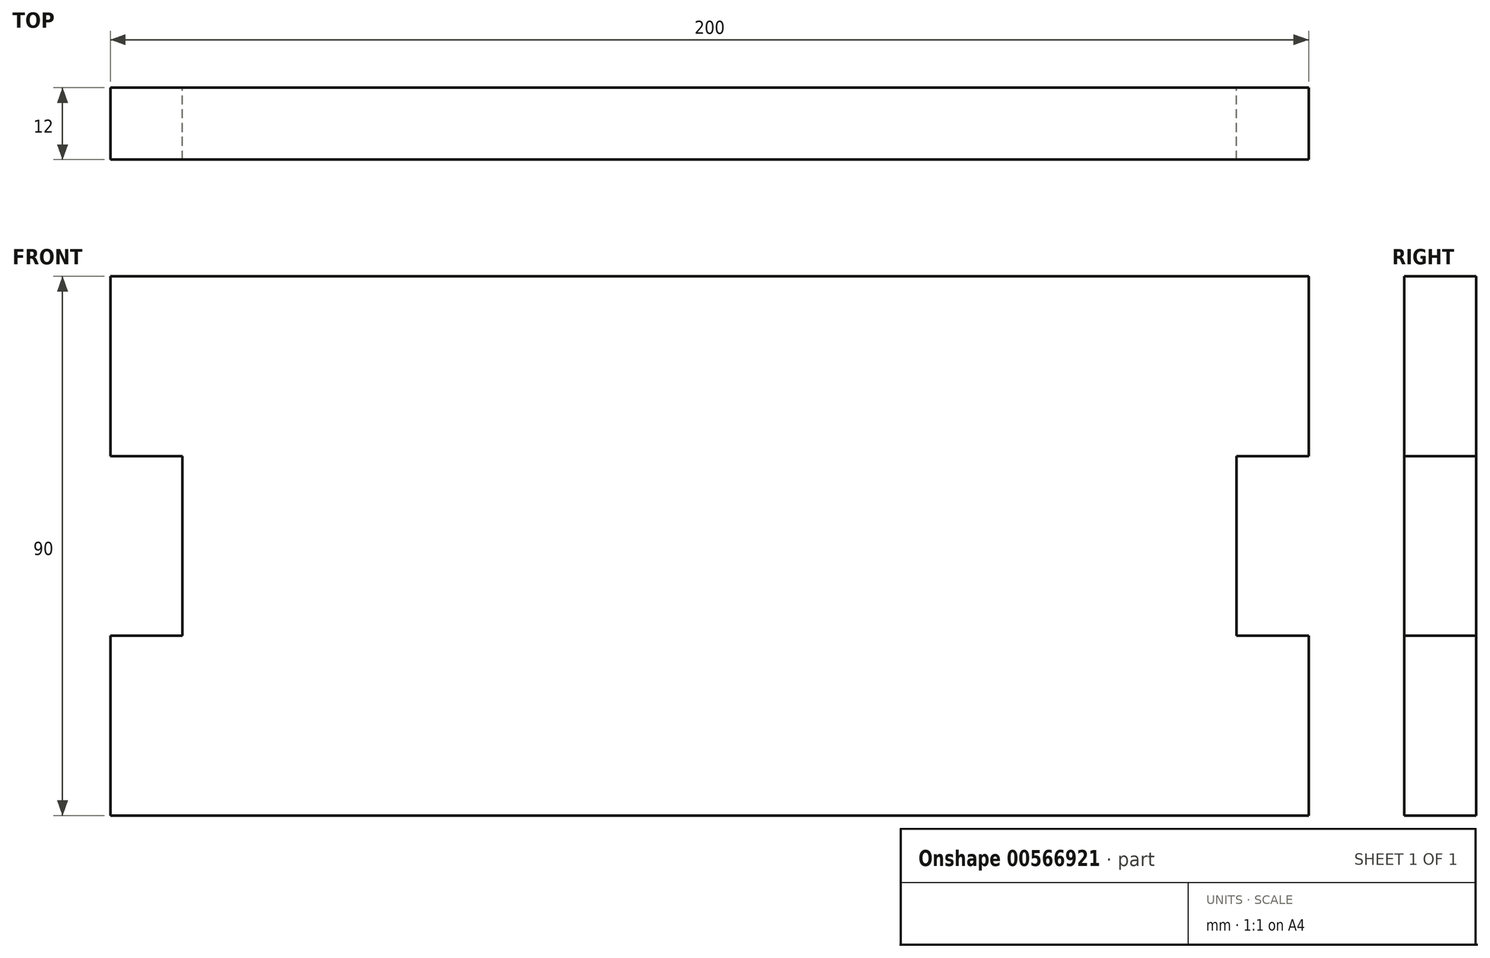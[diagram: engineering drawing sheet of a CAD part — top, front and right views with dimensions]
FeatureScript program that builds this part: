
annotation { "Feature Type Name" : "Feature", "Feature Type Description" : "" }
export const myFeature = defineFeature(function(context is Context, id is Id, definition is map)
    precondition{}
    {
        {
            var Q0;
            Q0=qCreatedBy(makeId("Front.planeOp"),FACE);
            var sketch = newSketch(context, id + "F0", { "sketchPlane" : qUnion([Q0])});
            skLineSegment(sketch, "E0", {"start": v(0, 0) * mm, "end": v(0, 30) * mm});
            skLineSegment(sketch, "E1", {"start": v(0, 30) * mm, "end": v(12, 30) * mm});
            skLineSegment(sketch, "E2", {"start": v(12, 30) * mm, "end": v(12, 60) * mm});
            skLineSegment(sketch, "E3", {"start": v(12, 60) * mm, "end": v(0, 60) * mm});
            skLineSegment(sketch, "E4", {"start": v(0, 60) * mm, "end": v(0, 90) * mm});
            skLineSegment(sketch, "E5", {"start": v(0, 90) * mm, "end": v(100, 90) * mm});
            skLineSegment(sketch, "E6", {"start": v(100, 90) * mm, "end": v(100, 0) * mm, "construction": true});
            skLineSegment(sketch, "E7", {"start": v(100, 0) * mm, "end": v(0, 0) * mm});
            skLineSegment(sketch, "E8.MirrorCS", {"start": v(200, 30) * mm, "end": v(188, 30) * mm});
            skLineSegment(sketch, "E9.MirrorCS", {"start": v(188, 30) * mm, "end": v(188, 60) * mm});
            skLineSegment(sketch, "E10.MirrorCS", {"start": v(200, 60) * mm, "end": v(200, 90) * mm});
            skLineSegment(sketch, "E11.MirrorCS", {"start": v(200, 0) * mm, "end": v(200, 30) * mm});
            skLineSegment(sketch, "E12.MirrorCS", {"start": v(200, 90) * mm, "end": v(100, 90) * mm});
            skLineSegment(sketch, "E13.MirrorCS", {"start": v(188, 60) * mm, "end": v(200, 60) * mm});
            skLineSegment(sketch, "E14.MirrorCS", {"start": v(100, 0) * mm, "end": v(200, 0) * mm});
            skSolve(sketch);
        }
        {
            var Q0;
            Q0=qSketchRegion(id+"F0",true);
            extrude(context, id + "F1", {"entities" : qUnion([Q0]), "depth" : 12 * mm, "offsetDistance" : 25 * mm});
        }
    });
